# Revit family: BE_50970.3_de_DE
name_source: partatom
category: Leuchten
units: mm (PartAtom-declared; Revit-internal decimal feet)

## family parameters
Basisbauteil = Fläche
Beim Laden mit Abzugskörper schneiden = Ja
Bemaßung runder Anschluss = Durchmesser verwenden
Gemeinsam genutzt = Nein
Lichtquelle = Nein
Raumberechnungspunkt = Ja
Teiletyp = Normal

## types (2) — shared parameters
Aktualisierung = 2023-11-09T04:00:03
BEGA_Dummy = Nein
BEGA_IES = Ja
BEGA_Intern = Ja
BEGA_Intern_Konstruktion = Ja
BEGA_Intern_an = Ja
BEGA_Intern_aus = Ja
Befestigungsabstand = 42 mm
Beschreibung = Systempendelleuchte
Beschreibung_Sonderanfertigung = Hier können Sie Informationen zur Sonderanfertigung eintragen.
CE_Konformität = ja
ENEC = ja
Energieeffizienzklasse = LED A++ - A
Farbwiedergabeindex = CRI > 90
Gewicht = 0.95 kg
Hersteller = BEGA
Lampe = LED 5.8 W
Lastklassifizierung = Beleuchtung
Lebensdauerkriterien = L80B50 @ ta 25 °C = 200000 h
Logo = BEGA_Logo.png
Material_11 = BEGA_Glas_opal
Material_18 = BEGA_Gummi_schwarz
Material_21 = BEGA_Oberfläche_Aluminium_poliert
Material_23 = BEGA_Oberfläche_Chrom_poliert
Material_35 = BEGA_Oberfläche_Samtschwarz_matt
Produktdatenblatt = https://cdn.bega.com
Scheinlast = 0 VA
Schutzart = IP 20
Schutzklasse = III
Sonderanfertigung = Nein
Spannung = 240 V
Strom = 0,35 A
URL = https://www.bega.com
Umgebungstemperatur = 25 °C
zero-valued in all types: Vorgabe-Ansicht

## per-type parameters (varying)
| type | BEGA_IES1 | BEGA_IES2 | Bestellnummer | Farbtemperatur | LED_Modulbezeichnung | Lampenlichtstrom | Leuchtenlichtstrom | Modell |
| BEGA_50970.3_K3 | Ja | Nein | 50970.3K3 | 3000 K | LED-1122/930 | 945 lm | 486 lm | 50970.3K3 |
| BEGA_50970.3_K4 | Nein | Ja | 50970.3K4 | 4000 K | LED-1122/940 | 1000 lm | 515 lm | 50970.3K4 |

## geometry (parser evidence)
native form markers: Blend x18, Sweep x3
no freeform markers — native parametric forms only
